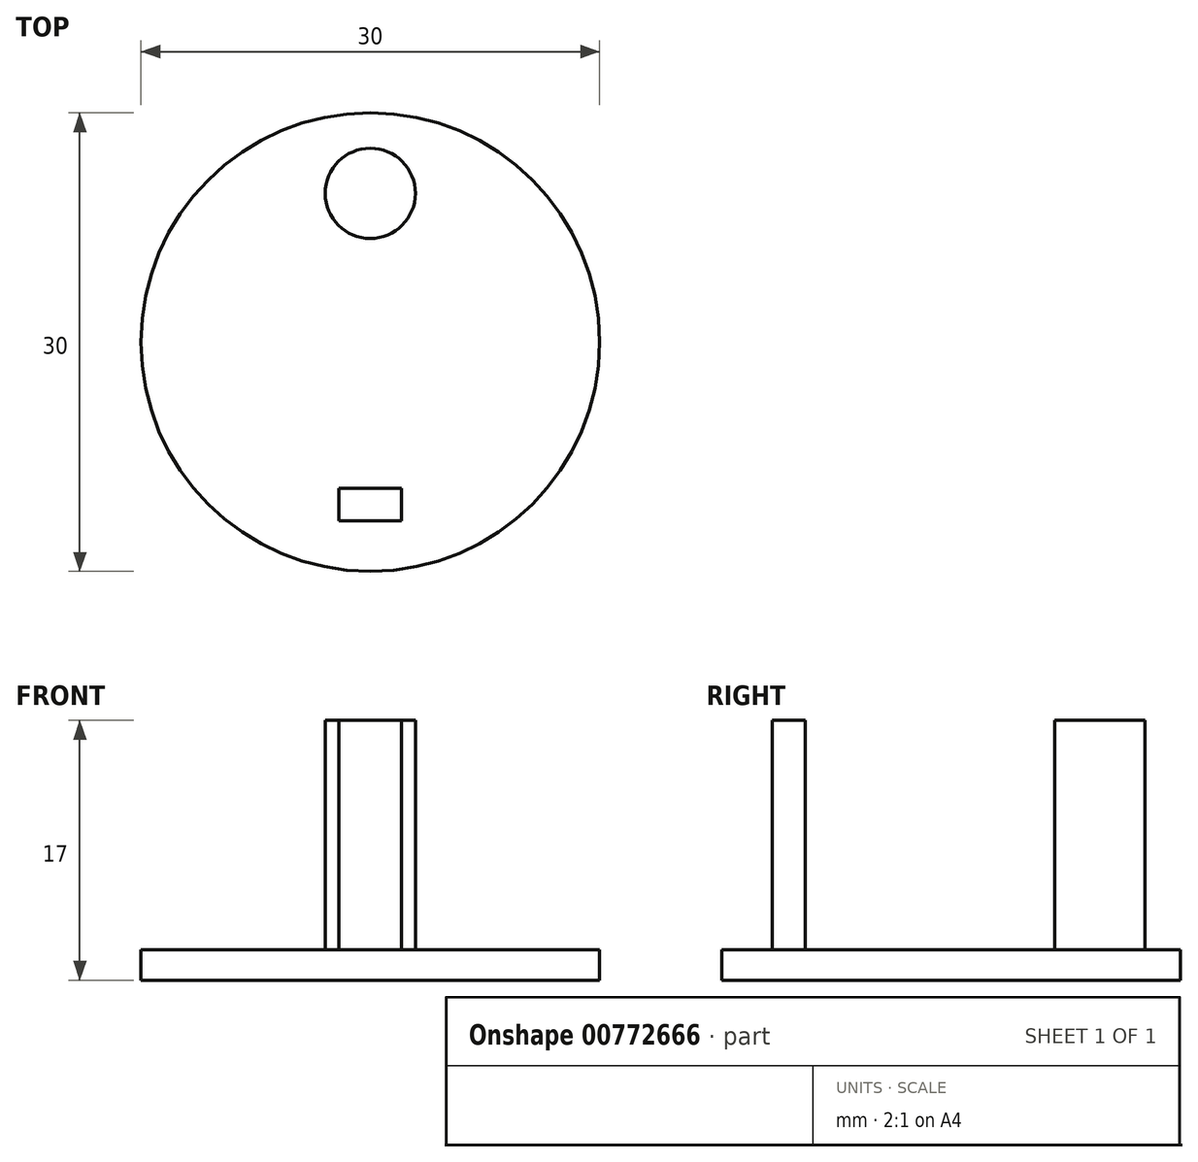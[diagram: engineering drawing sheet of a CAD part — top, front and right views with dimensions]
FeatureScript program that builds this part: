
annotation { "Feature Type Name" : "Feature", "Feature Type Description" : "" }
export const myFeature = defineFeature(function(context is Context, id is Id, definition is map)
    precondition{}
    {
        {
            var Q0;
            Q0=qCreatedBy(makeId("Top.planeOp"),FACE);
            var sketch = newSketch(context, id + "F0", { "sketchPlane" : qUnion([Q0])});
            skCircle(sketch, "E0", {"center": v(0, 0) * mm, "radius": 15 * mm});
            skSolve(sketch);
        }
        {
            var Q0;
            Q0=makeQuery(id+"F0.imprint","IMPRINT",FACE,{"disambiguationData":[TD([[makeQuery(id+"F0.imprint","IMPRINT",EDGE,{"derivedFrom":sQuery(id+"F0.wireOp",EDGE,"yiuzqnGU-mgO5-ho36-lMzk-z9wz4DCQD0MT.bottom")}),-1.0]])]});
            var Q1;
            Q1=makeQuery(id+"F0.imprint","IMPRINT",FACE,{"disambiguationData":[TD([[makeQuery(id+"F0.imprint","IMPRINT",EDGE,{"derivedFrom":sQuery(id+"F0.wireOp",EDGE,"E0")}),1.0]])]});
            extrude(context, id + "F1", {"entities" : qUnion([Q0, Q1]), "depth" : 2 * mm, "offsetDistance" : 25 * mm});
        }
        {
            var Q0;
            Q0=makeQuery(id+"F1.opExtrude","CAP_FACE",FACE,{"disambiguationData":[OSD([sQuery(id+"F0.wireOp",EDGE,"E0")])],"isStart":false});
            var sketch = newSketch(context, id + "F2", { "sketchPlane" : qUnion([Q0])});
            skCircle(sketch, "E1", {"center": v(0, 9.73) * mm, "radius": 2.95 * mm});
            skLineSegment(sketch, "E2.bottom", {"start": v(2.04, -9.56) * mm, "end": v(-2.04, -9.56) * mm});
            skLineSegment(sketch, "E2.top", {"start": v(2.04, -11.7) * mm, "end": v(-2.04, -11.7) * mm});
            skLineSegment(sketch, "E2.left", {"start": v(2.04, -9.56) * mm, "end": v(2.04, -11.7) * mm});
            skLineSegment(sketch, "E2.right", {"start": v(-2.04, -9.56) * mm, "end": v(-2.04, -11.7) * mm});
            skPoint(sketch, "E2.middle", {"position": v(0, -10.63) * mm});
            skSolve(sketch);
        }
        {
            var Q0;
            Q0 = qSketchRegion(id + "F2", true);
            extrude(context, id + "F3", {"entities" : qUnion([Q0]), "operationType" : NewBodyOperationType.ADD, "depth" : 15 * mm, "offsetDistance" : 25 * mm});
        }
    });
